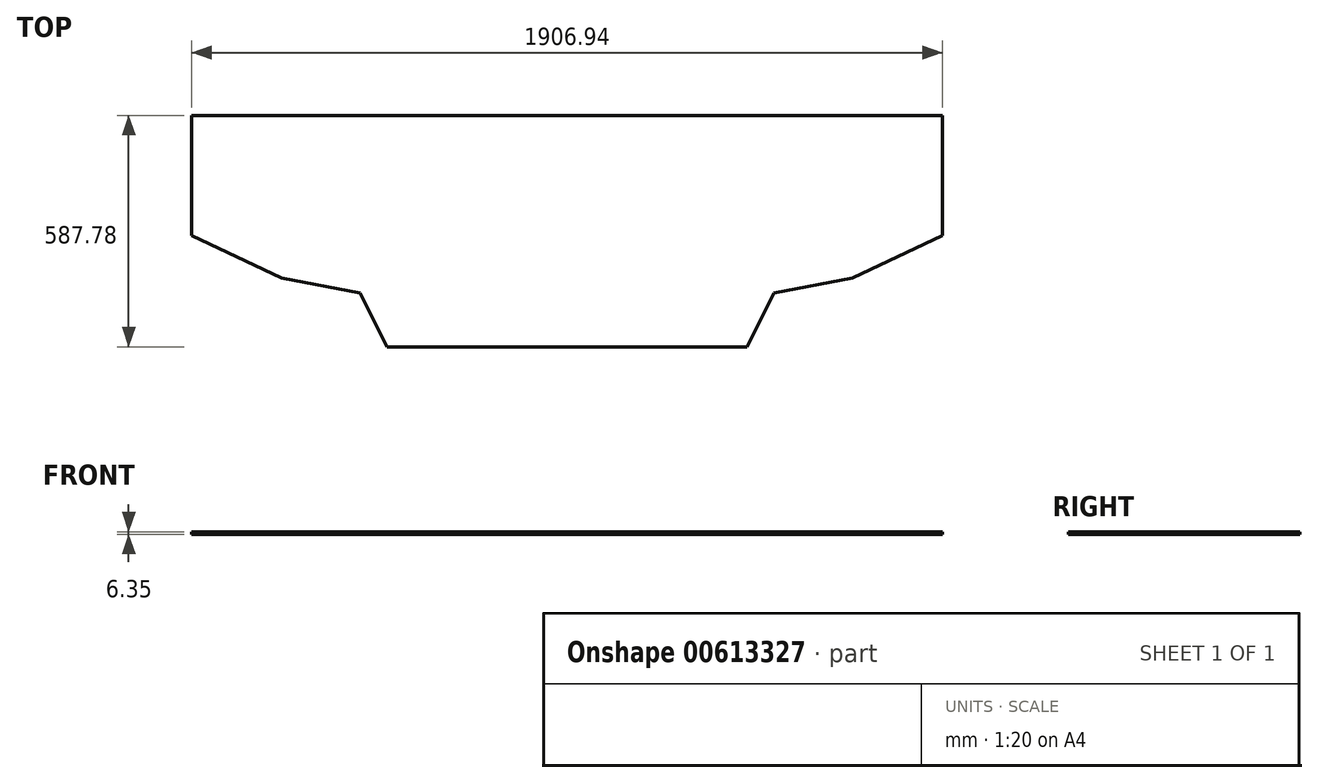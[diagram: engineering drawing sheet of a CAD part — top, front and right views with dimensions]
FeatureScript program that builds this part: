
annotation { "Feature Type Name" : "Feature", "Feature Type Description" : "" }
export const myFeature = defineFeature(function(context is Context, id is Id, definition is map)
    precondition{}
    {
        {
            var Q0;
            Q0=qCreatedBy(makeId("Top.planeOp"),FACE);
            var sketch = newSketch(context, id + "F0", { "sketchPlane" : qUnion([Q0])});
            skPoint(sketch, "E0.middle", {"position": v(0, 0) * mm});
            skLineSegment(sketch, "E1", {"start": v(-457.2, -152.4) * mm, "end": v(-525.44, -16.13) * mm});
            skLineSegment(sketch, "E2", {"start": v(-525.44, -16.13) * mm, "end": v(-724.84, 22.99) * mm});
            skLineSegment(sketch, "E3", {"start": v(-724.84, 22.99) * mm, "end": v(-953.47, 130.58) * mm});
            skLineSegment(sketch, "E4", {"start": v(-953.47, 130.58) * mm, "end": v(-953.47, 435.38) * mm});
            skLineSegment(sketch, "E5", {"start": v(0, -152.4) * mm, "end": v(0, 435.38) * mm});
            skLineSegment(sketch, "E6", {"start": v(0, 435.38) * mm, "end": v(-953.47, 435.38) * mm});
            skLineSegment(sketch, "E7", {"start": v(0, -152.4) * mm, "end": v(-457.2, -152.4) * mm});
            skSolve(sketch);
        }
        {
            var Q0;
            Q0 = qSketchRegion(id + "F0", true);
            var Q1;
            Q1=makeQuery(id+"F0.imprint","IMPRINT",FACE,{"disambiguationData":[TD([[makeQuery(id+"F0.imprint","IMPRINT",EDGE,{"derivedFrom":sQuery(id+"F0.wireOp",EDGE,"E1")}),-1.0]])]});
            extrude(context, id + "F1", {"entities" : qUnion([Q0, Q1]), "depth" : 6.35 * mm, "offsetDistance" : 25.4 * mm});
        }
        {
            var Q0;
            Q0=makeQuery(id+"F1.opExtrude","SWEPT_BODY",BODY,{"disambiguationData":[OSD([sQuery(id+"F0.wireOp",EDGE,"E1"),sQuery(id+"F0.wireOp",EDGE,"E2"),sQuery(id+"F0.wireOp",EDGE,"E3"),sQuery(id+"F0.wireOp",EDGE,"E4"),sQuery(id+"F0.wireOp",EDGE,"E5"),sQuery(id+"F0.wireOp",EDGE,"E6"),sQuery(id+"F0.wireOp",EDGE,"E7")])]});
            var Q1;
            Q1=qCreatedBy(makeId("Right.planeOp"),FACE);
            mirror(context, id + "F2", {"operationType" : NewBodyOperationType.ADD, "entities" : qUnion([Q0]), "mirrorPlane" : qUnion([Q1])});
        }
    });
